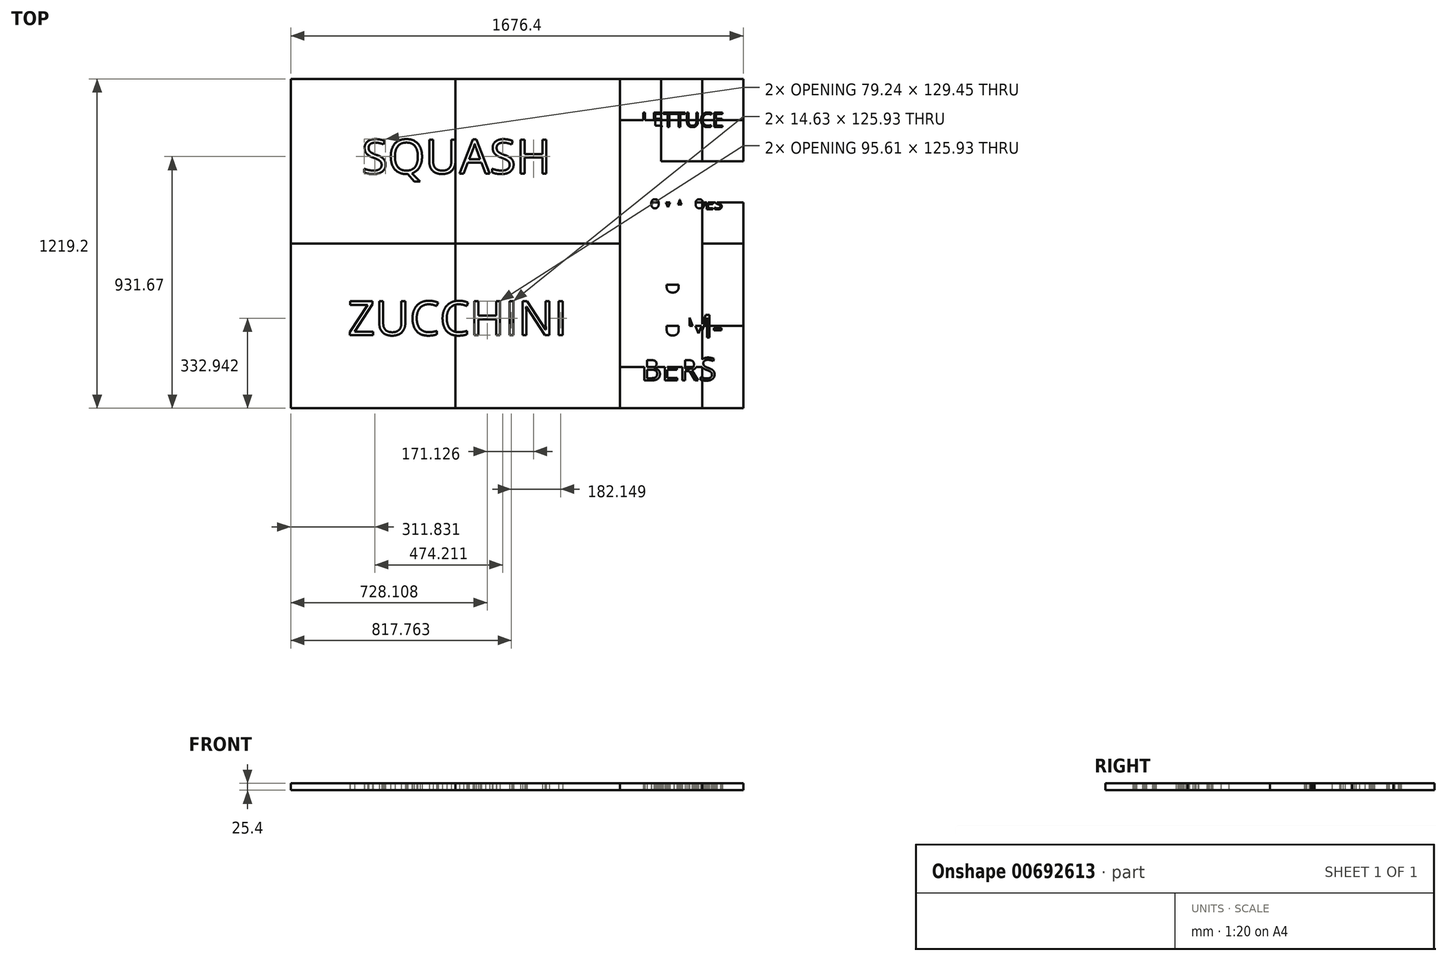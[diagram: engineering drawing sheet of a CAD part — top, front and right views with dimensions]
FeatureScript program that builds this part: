
annotation { "Feature Type Name" : "Feature", "Feature Type Description" : "" }
export const myFeature = defineFeature(function(context is Context, id is Id, definition is map)
    precondition{}
    {
        {
            var Q0;
            Q0=qCreatedBy(makeId("Top.planeOp"),FACE);
            var sketch = newSketch(context, id + "F0", { "sketchPlane" : qUnion([Q0])});
            skLineSegment(sketch, "E0.bottom", {"start": v(-653.67, 324.32) * mm, "end": v(-44.07, 324.32) * mm});
            skLineSegment(sketch, "E0.top", {"start": v(-653.67, -285.28) * mm, "end": v(-44.07, -285.28) * mm});
            skLineSegment(sketch, "E0.left", {"start": v(-653.67, 324.32) * mm, "end": v(-653.67, -285.28) * mm});
            skLineSegment(sketch, "E0.right", {"start": v(-44.07, 324.32) * mm, "end": v(-44.07, -285.28) * mm});
            skLineSegment(sketch, "E1.bottom", {"start": v(-44.07, 324.32) * mm, "end": v(565.53, 324.32) * mm});
            skLineSegment(sketch, "E1.top", {"start": v(-44.07, -285.28) * mm, "end": v(565.53, -285.28) * mm});
            skLineSegment(sketch, "E1.right", {"start": v(565.53, 324.32) * mm, "end": v(565.53, -285.28) * mm});
            skText(sketch, "E2", { "text": "SQUASH", "fontName": "OpenSans-Regular.ttf"});
            skLineSegment(sketch, "E3.0.1.0", {"start": v(565.53, -285.28) * mm, "end": v(565.53, -894.88) * mm});
            skLineSegment(sketch, "E3.0.1.1", {"start": v(-44.07, -285.28) * mm, "end": v(-44.07, -894.88) * mm});
            skLineSegment(sketch, "E3.0.1.2", {"start": v(-44.07, -894.88) * mm, "end": v(565.53, -894.88) * mm});
            skLineSegment(sketch, "E3.0.1.4", {"start": v(-653.67, -285.28) * mm, "end": v(-653.67, -894.88) * mm});
            skLineSegment(sketch, "E3.0.1.5", {"start": v(-653.67, -894.88) * mm, "end": v(-44.07, -894.88) * mm});
            skLineSegment(sketch, "E3.0.1.7", {"start": v(-44.07, -285.28) * mm, "end": v(-44.07, -894.88) * mm});
            skLineSegment(sketch, "E3.direction1", {"start": v(-653.67, -285.28) * mm, "end": v(-636.4, -285.28) * mm, "construction": true});
            skLineSegment(sketch, "E3.direction2", {"start": v(-653.67, -285.28) * mm, "end": v(-653.67, -894.88) * mm, "construction": true});
            skText(sketch, "E4", { "text": "ZUCCHINI", "fontName": "OpenSans-Regular.ttf"});
            skLineSegment(sketch, "E5.bottom", {"start": v(565.53, 324.32) * mm, "end": v(717.93, 324.32) * mm});
            skLineSegment(sketch, "E5.top", {"start": v(565.53, 171.92) * mm, "end": v(717.93, 171.92) * mm});
            skLineSegment(sketch, "E5.left", {"start": v(565.53, 324.32) * mm, "end": v(565.53, 171.92) * mm});
            skLineSegment(sketch, "E5.right", {"start": v(717.93, 324.32) * mm, "end": v(717.93, 171.92) * mm});
            skLineSegment(sketch, "E6.top", {"start": v(565.53, 19.52) * mm, "end": v(717.93, 19.52) * mm});
            skLineSegment(sketch, "E6.left", {"start": v(565.53, 171.92) * mm, "end": v(565.53, 19.52) * mm});
            skLineSegment(sketch, "E6.right", {"start": v(717.93, 171.92) * mm, "end": v(717.93, 19.52) * mm});
            skLineSegment(sketch, "E7.bottom", {"start": v(870.33, 324.32) * mm, "end": v(1022.73, 324.32) * mm});
            skLineSegment(sketch, "E7.top", {"start": v(870.33, 171.92) * mm, "end": v(1022.73, 171.92) * mm});
            skLineSegment(sketch, "E7.left", {"start": v(870.33, 324.32) * mm, "end": v(870.33, 171.92) * mm});
            skLineSegment(sketch, "E7.right", {"start": v(1022.73, 324.32) * mm, "end": v(1022.73, 171.92) * mm});
            skLineSegment(sketch, "E8.bottom", {"start": v(717.93, 324.32) * mm, "end": v(870.33, 324.32) * mm});
            skLineSegment(sketch, "E8.top", {"start": v(717.93, 171.92) * mm, "end": v(870.33, 171.92) * mm});
            skLineSegment(sketch, "E9.top", {"start": v(717.93, 19.52) * mm, "end": v(870.33, 19.52) * mm});
            skLineSegment(sketch, "E9.right", {"start": v(870.33, 171.92) * mm, "end": v(870.33, 19.52) * mm});
            skLineSegment(sketch, "E10.top", {"start": v(870.33, 19.52) * mm, "end": v(1022.73, 19.52) * mm});
            skLineSegment(sketch, "E10.right", {"start": v(1022.73, 171.92) * mm, "end": v(1022.73, 19.52) * mm});
            skText(sketch, "E11", { "text": "LETTUCE", "fontName": "OpenSans-Regular.ttf"});
            skPoint(sketch, "E11.secondSnap0", {"position": v(870.79, 146.52) * mm});
            skLineSegment(sketch, "E12.0.1.0", {"start": v(870.33, -132.88) * mm, "end": v(1022.73, -132.88) * mm});
            skLineSegment(sketch, "E12.0.1.1", {"start": v(870.33, 19.52) * mm, "end": v(870.33, -132.88) * mm});
            skLineSegment(sketch, "E12.0.1.3", {"start": v(1022.73, -132.88) * mm, "end": v(1022.73, -285.28) * mm});
            skLineSegment(sketch, "E12.0.1.4", {"start": v(717.93, -132.88) * mm, "end": v(717.93, -285.28) * mm});
            skLineSegment(sketch, "E12.0.1.5", {"start": v(717.93, 19.52) * mm, "end": v(717.93, -132.88) * mm});
            skLineSegment(sketch, "E12.0.1.6", {"start": v(870.33, -132.88) * mm, "end": v(870.33, -285.28) * mm});
            skLineSegment(sketch, "E12.0.1.7", {"start": v(870.33, -285.28) * mm, "end": v(1022.73, -285.28) * mm});
            skPoint(sketch, "E12.0.1.8", {"position": v(870.79, -158.28) * mm});
            skLineSegment(sketch, "E12.0.1.9", {"start": v(717.93, -285.28) * mm, "end": v(870.33, -285.28) * mm});
            skLineSegment(sketch, "E12.0.1.10", {"start": v(717.93, -132.88) * mm, "end": v(870.33, -132.88) * mm});
            skLineSegment(sketch, "E12.0.1.12", {"start": v(1022.73, 19.52) * mm, "end": v(1022.73, -132.88) * mm});
            skLineSegment(sketch, "E12.0.1.13", {"start": v(870.33, -132.88) * mm, "end": v(870.33, -285.28) * mm});
            skLineSegment(sketch, "E12.0.1.14", {"start": v(870.33, -132.88) * mm, "end": v(1022.73, -132.88) * mm});
            skLineSegment(sketch, "E12.0.1.15", {"start": v(717.93, -132.88) * mm, "end": v(717.93, -285.28) * mm});
            skLineSegment(sketch, "E12.0.1.16", {"start": v(870.33, 19.52) * mm, "end": v(870.33, -132.88) * mm});
            skLineSegment(sketch, "E12.0.1.17", {"start": v(717.93, 19.52) * mm, "end": v(717.93, -132.88) * mm});
            skLineSegment(sketch, "E12.0.1.18", {"start": v(717.93, -132.88) * mm, "end": v(870.33, -132.88) * mm});
            skLineSegment(sketch, "E12.0.1.20", {"start": v(565.53, -132.88) * mm, "end": v(717.93, -132.88) * mm});
            skLineSegment(sketch, "E12.0.1.21", {"start": v(565.53, -132.88) * mm, "end": v(565.53, -285.28) * mm});
            skLineSegment(sketch, "E12.0.1.22", {"start": v(565.53, -285.28) * mm, "end": v(717.93, -285.28) * mm});
            skLineSegment(sketch, "E12.0.1.23", {"start": v(565.53, 19.52) * mm, "end": v(565.53, -132.88) * mm});
            skLineSegment(sketch, "E12.0.1.24", {"start": v(565.53, -132.88) * mm, "end": v(717.93, -132.88) * mm});
            skLineSegment(sketch, "E12.direction1", {"start": v(565.53, 19.52) * mm, "end": v(591.39, 19.52) * mm, "construction": true});
            skLineSegment(sketch, "E12.direction2", {"start": v(565.53, 19.52) * mm, "end": v(565.53, -285.28) * mm, "construction": true});
            skText(sketch, "E13", { "text": "TOMATOES", "fontName": "OpenSans-Regular.ttf"});
            skPoint(sketch, "E14", {"position": v(794.13, -132.88) * mm});
            skLineSegment(sketch, "E15.bottom", {"start": v(565.53, -285.28) * mm, "end": v(870.33, -285.28) * mm});
            skLineSegment(sketch, "E15.top", {"start": v(565.53, -437.68) * mm, "end": v(870.33, -437.68) * mm});
            skLineSegment(sketch, "E15.left", {"start": v(565.53, -285.28) * mm, "end": v(565.53, -437.68) * mm});
            skLineSegment(sketch, "E15.right", {"start": v(870.33, -285.28) * mm, "end": v(870.33, -437.68) * mm});
            skLineSegment(sketch, "E16.top", {"start": v(565.53, -590.08) * mm, "end": v(870.33, -590.08) * mm});
            skLineSegment(sketch, "E16.left", {"start": v(565.53, -437.68) * mm, "end": v(565.53, -590.08) * mm});
            skLineSegment(sketch, "E16.right", {"start": v(870.33, -437.68) * mm, "end": v(870.33, -590.08) * mm});
            skLineSegment(sketch, "E17.top", {"start": v(565.53, -742.48) * mm, "end": v(870.33, -742.48) * mm});
            skLineSegment(sketch, "E17.left", {"start": v(565.53, -590.08) * mm, "end": v(565.53, -742.48) * mm});
            skLineSegment(sketch, "E17.right", {"start": v(870.33, -590.08) * mm, "end": v(870.33, -742.48) * mm});
            skLineSegment(sketch, "E18.top", {"start": v(565.53, -894.88) * mm, "end": v(870.33, -894.88) * mm});
            skLineSegment(sketch, "E18.left", {"start": v(565.53, -742.48) * mm, "end": v(565.53, -894.88) * mm});
            skLineSegment(sketch, "E18.right", {"start": v(870.33, -742.48) * mm, "end": v(870.33, -894.88) * mm});
            skLineSegment(sketch, "E19.top", {"start": v(870.33, -590.08) * mm, "end": v(1022.73, -590.08) * mm});
            skLineSegment(sketch, "E19.left", {"start": v(870.33, -285.28) * mm, "end": v(870.33, -590.08) * mm});
            skLineSegment(sketch, "E19.right", {"start": v(1022.73, -285.28) * mm, "end": v(1022.73, -590.08) * mm});
            skLineSegment(sketch, "E20.top", {"start": v(870.33, -894.88) * mm, "end": v(1022.73, -894.88) * mm});
            skLineSegment(sketch, "E20.left", {"start": v(870.33, -590.08) * mm, "end": v(870.33, -894.88) * mm});
            skLineSegment(sketch, "E20.right", {"start": v(1022.73, -590.08) * mm, "end": v(1022.73, -894.88) * mm});
            skText(sketch, "E21", { "text": "CU-\nCUM-\nBERS", "fontName": "OpenSans-Regular.ttf"});
            const initialGuessF0  = {"E2": [-0.39058, -0.0262, 1, 0, 0.127], "E4": [-0.44234, -0.6249, 1, 0, 0.127], "E11": [0.64538, 0.14652, 1, 0, 0.0535], "E13": [0.64173, -0.15828, 1, 0, 0.04124], "E21": [0.645, -0.47423, 1, 0, 0.08417]};
            skSetInitialGuess(sketch, initialGuessF0);
            skSolve(sketch);
        }
        {
            var Q0;
            {var subQ5=sQuery(id+"F0.wireOp",EDGE,"E0.bottom");Q0=makeQuery(id+"F0.imprint","IMPRINT",FACE,{"disambiguationData":[TD([[makeQuery(id+"F0.imprint","IMPRINT",EDGE,{"derivedFrom":subQ5}),-1.0]])]});}
            var Q1;
            Q1=makeQuery(id+"F0.imprint","IMPRINT",FACE,{"disambiguationData":[TD([[makeQuery(id+"F0.imprint","IMPRINT",EDGE,{"derivedFrom":sQuery(id+"F0.wireOp",EDGE,"E2.sketch_text.stroke-37")}),1.0]])]});
            extrude(context, id + "F1", {"entities" : qUnion([Q0, Q1]), "depth" : 25.4 * mm, "offsetDistance" : 25.4 * mm});
        }
        {
            var Q0;
            Q0=makeQuery(id+"F0.imprint","IMPRINT",FACE,{"disambiguationData":[TD([[makeQuery(id+"F0.imprint","IMPRINT",EDGE,{"derivedFrom":sQuery(id+"F0.wireOp",EDGE,"E2.sketch_text.stroke-67")}),1.0]])]});
            var Q1;
            {var subQ4=sQuery(id+"F0.wireOp",EDGE,"E1.bottom");Q1=makeQuery(id+"F0.imprint","IMPRINT",FACE,{"disambiguationData":[TD([[makeQuery(id+"F0.imprint","IMPRINT",EDGE,{"derivedFrom":subQ4}),-1.0]])]});}
            extrude(context, id + "F2", {"entities" : qUnion([Q0, Q1]), "depth" : 25.4 * mm, "offsetDistance" : 25.4 * mm});
        }
        {
            var Q0;
            {var subQ0=sQuery(id+"F0.wireOp",EDGE,"E4.sketch_text.stroke-40");Q0=makeQuery(id+"F0.imprint","IMPRINT",FACE,{"disambiguationData":[TD([[makeQuery(id+"F0.imprint","IMPRINT",EDGE,{"derivedFrom":subQ0}),1.0]])]});}
            var Q1;
            Q1=makeQuery(id+"F0.imprint","IMPRINT",FACE,{"disambiguationData":[TD([[makeQuery(id+"F0.imprint","IMPRINT",EDGE,{"derivedFrom":sQuery(id+"F0.wireOp",EDGE,"E3.0.1.4")}),1.0]])]});
            extrude(context, id + "F3", {"entities" : qUnion([Q0, Q1]), "depth" : 25.4 * mm, "offsetDistance" : 25.4 * mm});
        }
        {
            var Q0;
            {var subQ1=sQuery(id+"F0.wireOp",EDGE,"E3.0.1.2");Q0=makeQuery(id+"F0.imprint","IMPRINT",FACE,{"disambiguationData":[TD([[makeQuery(id+"F0.imprint","IMPRINT",EDGE,{"derivedFrom":subQ1}),1.0]])]});}
            extrude(context, id + "F4", {"entities" : qUnion([Q0]), "depth" : 25.4 * mm, "offsetDistance" : 25.4 * mm});
        }
        {
            var Q0;
            {var subQ5=sQuery(id+"F0.wireOp",EDGE,"E11.sketch_text.stroke-11");Q0=makeQuery(id+"F0.imprint","IMPRINT",FACE,{"disambiguationData":[TD([[makeQuery(id+"F0.imprint","IMPRINT",EDGE,{"derivedFrom":subQ5}),1.0]])]});}
            var Q1;
            {var subQ8=sQuery(id+"F0.wireOp",EDGE,"E5.bottom");Q1=makeQuery(id+"F0.imprint","IMPRINT",FACE,{"disambiguationData":[TD([[makeQuery(id+"F0.imprint","IMPRINT",EDGE,{"derivedFrom":subQ8}),-1.0]])]});}
            extrude(context, id + "F5", {"entities" : qUnion([Q0, Q1]), "depth" : 25.4 * mm, "offsetDistance" : 25.4 * mm});
        }
        {
            var Q0;
            {var subQ26=sQuery(id+"F0.wireOp",EDGE,"E8.bottom");Q0=makeQuery(id+"F0.imprint","IMPRINT",FACE,{"disambiguationData":[TD([[makeQuery(id+"F0.imprint","IMPRINT",EDGE,{"derivedFrom":subQ26}),-1.0]])]});}
            extrude(context, id + "F6", {"entities" : qUnion([Q0]), "depth" : 25.4 * mm, "offsetDistance" : 25.4 * mm});
        }
        {
            var Q0;
            {var subQ10=sQuery(id+"F0.wireOp",EDGE,"E7.bottom");Q0=makeQuery(id+"F0.imprint","IMPRINT",FACE,{"disambiguationData":[TD([[makeQuery(id+"F0.imprint","IMPRINT",EDGE,{"derivedFrom":subQ10}),-1.0]])]});}
            extrude(context, id + "F7", {"entities" : qUnion([Q0]), "depth" : 25.4 * mm, "offsetDistance" : 25.4 * mm});
        }
        {
            var Q0;
            {var subQ5=sQuery(id+"F0.wireOp",EDGE,"E11.sketch_text.stroke-15");Q0=makeQuery(id+"F0.imprint","IMPRINT",FACE,{"disambiguationData":[TD([[makeQuery(id+"F0.imprint","IMPRINT",EDGE,{"derivedFrom":subQ5}),1.0]])]});}
            var Q1;
            {var subQ12=sQuery(id+"F0.wireOp",EDGE,"E6.left");Q1=makeQuery(id+"F0.imprint","IMPRINT",FACE,{"disambiguationData":[TD([[makeQuery(id+"F0.imprint","IMPRINT",EDGE,{"derivedFrom":subQ12}),1.0]])]});}
            extrude(context, id + "F8", {"entities" : qUnion([Q0, Q1]), "depth" : 25.4 * mm, "offsetDistance" : 25.4 * mm});
        }
        {
            var Q0;
            {var subQ0=sQuery(id+"F0.wireOp",EDGE,"E11.sketch_text.stroke-42");Q0=makeQuery(id+"F0.imprint","IMPRINT",FACE,{"disambiguationData":[TD([[makeQuery(id+"F0.imprint","IMPRINT",EDGE,{"derivedFrom":subQ0}),1.0]])]});}
            var Q1;
            {var subQ20=sQuery(id+"F0.wireOp",EDGE,"E11.sketch_text.stroke-17");Q1=makeQuery(id+"F0.imprint","IMPRINT",FACE,{"disambiguationData":[TD([[makeQuery(id+"F0.imprint","IMPRINT",EDGE,{"derivedFrom":subQ20}),1.0]])]});}
            extrude(context, id + "F9", {"entities" : qUnion([Q0, Q1]), "depth" : 25.4 * mm, "offsetDistance" : 25.4 * mm});
        }
        {
            var Q0;
            {var subQ11=sQuery(id+"F0.wireOp",EDGE,"E10.right");Q0=makeQuery(id+"F0.imprint","IMPRINT",FACE,{"disambiguationData":[TD([[makeQuery(id+"F0.imprint","IMPRINT",EDGE,{"derivedFrom":subQ11}),-1.0]])]});}
            extrude(context, id + "F10", {"entities" : qUnion([Q0]), "depth" : 25.4 * mm, "offsetDistance" : 25.4 * mm});
        }
        {
            var Q0;
            {var subQ0=sQuery(id+"F0.wireOp",EDGE,"E13.sketch_text.stroke-21");Q0=makeQuery(id+"F0.imprint","IMPRINT",FACE,{"disambiguationData":[TD([[makeQuery(id+"F0.imprint","IMPRINT",EDGE,{"derivedFrom":subQ0}),1.0]])]});}
            var Q1;
            {var subQ4=sQuery(id+"F0.wireOp",EDGE,"E12.0.1.17");Q1=makeQuery(id+"F0.imprint","IMPRINT",FACE,{"disambiguationData":[TD([[makeQuery(id+"F0.imprint","IMPRINT",EDGE,{"derivedFrom":subQ4}),-1.0]])]});}
            extrude(context, id + "F11", {"entities" : qUnion([Q0, Q1]), "depth" : 25.4 * mm, "offsetDistance" : 25.4 * mm});
        }
        {
            var Q0;
            {var subQ1=sQuery(id+"F0.wireOp",EDGE,"E13.sketch_text.stroke-51");Q0=makeQuery(id+"F0.imprint","IMPRINT",FACE,{"disambiguationData":[TD([[makeQuery(id+"F0.imprint","IMPRINT",EDGE,{"derivedFrom":subQ1}),1.0]])]});}
            var Q1;
            {var subQ18=sQuery(id+"F0.wireOp",EDGE,"E9.top");Q1=makeQuery(id+"F0.imprint","IMPRINT",FACE,{"disambiguationData":[TD([[makeQuery(id+"F0.imprint","IMPRINT",EDGE,{"derivedFrom":subQ18}),-1.0]])]});}
            var Q2;
            {var subQ0=sQuery(id+"F0.wireOp",EDGE,"E13.sketch_text.stroke-76");Q2=makeQuery(id+"F0.imprint","IMPRINT",FACE,{"disambiguationData":[TD([[makeQuery(id+"F0.imprint","IMPRINT",EDGE,{"derivedFrom":subQ0}),1.0]])]});}
            extrude(context, id + "F12", {"entities" : qUnion([Q0, Q1, Q2]), "depth" : 25.4 * mm, "offsetDistance" : 25.4 * mm});
        }
        {
            var Q0;
            {var subQ1=sQuery(id+"F0.wireOp",EDGE,"E12.0.1.14");var subQ3=sQuery(id+"F0.wireOp",EDGE,"E13.sketch_text.stroke-75");var subQ4=makeQuery(id+"F0.imprint","INTERSECT",VERTEX,{"derivedFrom":[subQ1,subQ3]});Q0=makeQuery(id+"F0.imprint","IMPRINT",FACE,{"disambiguationData":[TD([[makeQuery(id+"F0.imprint","IMPRINT",EDGE,{"disambiguationData":[TD([[subQ4,-1.0]])],"derivedFrom":subQ3}),1.0]])]});}
            var Q1;
            {var subQ1=sQuery(id+"F0.wireOp",EDGE,"E10.top");Q1=makeQuery(id+"F0.imprint","IMPRINT",FACE,{"disambiguationData":[TD([[makeQuery(id+"F0.imprint","IMPRINT",EDGE,{"derivedFrom":subQ1}),-1.0]])]});}
            extrude(context, id + "F13", {"entities" : qUnion([Q0, Q1]), "depth" : 25.4 * mm, "offsetDistance" : 25.4 * mm});
        }
        {
            var Q0;
            {var subQ0=sQuery(id+"F0.wireOp",EDGE,"E13.sketch_text.stroke-16");Q0=makeQuery(id+"F0.imprint","IMPRINT",FACE,{"disambiguationData":[TD([[makeQuery(id+"F0.imprint","IMPRINT",EDGE,{"derivedFrom":subQ0}),1.0]])]});}
            var Q1;
            {var subQ7=sQuery(id+"F0.wireOp",EDGE,"E12.0.1.15");Q1=makeQuery(id+"F0.imprint","IMPRINT",FACE,{"disambiguationData":[TD([[makeQuery(id+"F0.imprint","IMPRINT",EDGE,{"derivedFrom":subQ7}),-1.0]])]});}
            var Q2;
            {var subQ3=sQuery(id+"F0.wireOp",EDGE,"E13.sketch_text.stroke-74");var subQ5=sQuery(id+"F0.wireOp",EDGE,"E13.sketch_text.stroke-75");var subQ7=makeQuery(id+"F0.imprint","INTERSECT",VERTEX,{"derivedFrom":[subQ3,subQ5]});Q2=makeQuery(id+"F0.imprint","IMPRINT",FACE,{"disambiguationData":[TD([[makeQuery(id+"F0.imprint","IMPRINT",EDGE,{"disambiguationData":[TD([[subQ7,1.0]])],"derivedFrom":subQ3}),1.0]])]});}
            var Q3;
            {var subQ11=sQuery(id+"F0.wireOp",EDGE,"E12.0.1.3");Q3=makeQuery(id+"F0.imprint","IMPRINT",FACE,{"disambiguationData":[TD([[makeQuery(id+"F0.imprint","IMPRINT",EDGE,{"derivedFrom":subQ11}),-1.0]])]});}
            var Q4;
            {var subQ0=sQuery(id+"F0.wireOp",EDGE,"E21.sketch_text.stroke-23");Q4=makeQuery(id+"F0.imprint","IMPRINT",FACE,{"disambiguationData":[TD([[makeQuery(id+"F0.imprint","IMPRINT",EDGE,{"derivedFrom":subQ0}),1.0]])]});}
            var Q5;
            {var subQ26=sQuery(id+"F0.wireOp",EDGE,"E16.left");Q5=makeQuery(id+"F0.imprint","IMPRINT",FACE,{"disambiguationData":[TD([[makeQuery(id+"F0.imprint","IMPRINT",EDGE,{"derivedFrom":subQ26}),1.0]])]});}
            var Q6;
            Q6=makeQuery(id+"F0.imprint","IMPRINT",FACE,{"disambiguationData":[TD([[makeQuery(id+"F0.imprint","IMPRINT",EDGE,{"derivedFrom":sQuery(id+"F0.wireOp",EDGE,"E21.sketch_text.stroke-102")}),1.0]])]});
            var Q7;
            {var subQ6=sQuery(id+"F0.wireOp",EDGE,"E21.sketch_text.stroke-132");Q7=makeQuery(id+"F0.imprint","IMPRINT",FACE,{"disambiguationData":[TD([[makeQuery(id+"F0.imprint","IMPRINT",EDGE,{"derivedFrom":subQ6}),1.0]])]});}
            var Q8;
            {var subQ25=sQuery(id+"F0.wireOp",EDGE,"E18.top");Q8=makeQuery(id+"F0.imprint","IMPRINT",FACE,{"disambiguationData":[TD([[makeQuery(id+"F0.imprint","IMPRINT",EDGE,{"derivedFrom":subQ25}),1.0]])]});}
            extrude(context, id + "F14", {"entities" : qUnion([Q0, Q1, Q2, Q3, Q4, Q5, Q6, Q7, Q8]), "depth" : 25.4 * mm, "offsetDistance" : 25.4 * mm});
        }
        {
            var Q0;
            {var subQ5=sQuery(id+"F0.wireOp",EDGE,"E13.sketch_text.stroke-54");Q0=makeQuery(id+"F0.imprint","IMPRINT",FACE,{"disambiguationData":[TD([[makeQuery(id+"F0.imprint","IMPRINT",EDGE,{"derivedFrom":subQ5}),1.0]])]});}
            var Q1;
            {var subQ0=sQuery(id+"F0.wireOp",EDGE,"E13.sketch_text.stroke-71");Q1=makeQuery(id+"F0.imprint","IMPRINT",FACE,{"disambiguationData":[TD([[makeQuery(id+"F0.imprint","IMPRINT",EDGE,{"derivedFrom":subQ0}),1.0]])]});}
            var Q2;
            {var subQ4=sQuery(id+"F0.wireOp",EDGE,"E12.0.1.15");Q2=makeQuery(id+"F0.imprint","IMPRINT",FACE,{"disambiguationData":[TD([[makeQuery(id+"F0.imprint","IMPRINT",EDGE,{"derivedFrom":subQ4}),1.0]])]});}
            var Q3;
            {var subQ1=sQuery(id+"F0.wireOp",EDGE,"E21.sketch_text.stroke-76");Q3=makeQuery(id+"F0.imprint","IMPRINT",FACE,{"disambiguationData":[TD([[makeQuery(id+"F0.imprint","IMPRINT",EDGE,{"derivedFrom":subQ1}),1.0]])]});}
            var Q4;
            {var subQ5=sQuery(id+"F0.wireOp",EDGE,"E12.0.1.7");Q4=makeQuery(id+"F0.imprint","IMPRINT",FACE,{"disambiguationData":[TD([[makeQuery(id+"F0.imprint","IMPRINT",EDGE,{"derivedFrom":subQ5}),-1.0]])]});}
            var Q5;
            {var subQ0=sQuery(id+"F0.wireOp",EDGE,"E21.sketch_text.stroke-97");Q5=makeQuery(id+"F0.imprint","IMPRINT",FACE,{"disambiguationData":[TD([[makeQuery(id+"F0.imprint","IMPRINT",EDGE,{"derivedFrom":subQ0}),1.0]])]});}
            var Q6;
            {var subQ0=sQuery(id+"F0.wireOp",EDGE,"E21.sketch_text.stroke-135");Q6=makeQuery(id+"F0.imprint","IMPRINT",FACE,{"disambiguationData":[TD([[makeQuery(id+"F0.imprint","IMPRINT",EDGE,{"derivedFrom":subQ0}),1.0]])]});}
            var Q7;
            {var subQ0=sQuery(id+"F0.wireOp",EDGE,"E21.sketch_text.stroke-56");Q7=makeQuery(id+"F0.imprint","IMPRINT",FACE,{"disambiguationData":[TD([[makeQuery(id+"F0.imprint","IMPRINT",EDGE,{"derivedFrom":subQ0}),1.0]])]});}
            var Q8;
            {var subQ34=sQuery(id+"F0.wireOp",EDGE,"E17.left");Q8=makeQuery(id+"F0.imprint","IMPRINT",FACE,{"disambiguationData":[TD([[makeQuery(id+"F0.imprint","IMPRINT",EDGE,{"derivedFrom":subQ34}),1.0]])]});}
            var Q9;
            {var subQ5=sQuery(id+"F0.wireOp",EDGE,"E13.sketch_text.stroke-32");Q9=makeQuery(id+"F0.imprint","IMPRINT",FACE,{"disambiguationData":[TD([[makeQuery(id+"F0.imprint","IMPRINT",EDGE,{"derivedFrom":subQ5}),1.0]])]});}
            extrude(context, id + "F15", {"entities" : qUnion([Q0, Q1, Q2, Q3, Q4, Q5, Q6, Q7, Q8, Q9]), "depth" : 25.4 * mm, "offsetDistance" : 25.4 * mm});
        }
        {
            var Q0;
            {var subQ1=sQuery(id+"F0.wireOp",EDGE,"E21.sketch_text.stroke-63");Q0=makeQuery(id+"F0.imprint","IMPRINT",FACE,{"disambiguationData":[TD([[makeQuery(id+"F0.imprint","IMPRINT",EDGE,{"derivedFrom":subQ1}),1.0]])]});}
            var Q1;
            {var subQ5=sQuery(id+"F0.wireOp",EDGE,"E21.sketch_text.stroke-70");Q1=makeQuery(id+"F0.imprint","IMPRINT",FACE,{"disambiguationData":[TD([[makeQuery(id+"F0.imprint","IMPRINT",EDGE,{"derivedFrom":subQ5}),1.0]])]});}
            var Q2;
            {var subQ11=sQuery(id+"F0.wireOp",EDGE,"E20.top");Q2=makeQuery(id+"F0.imprint","IMPRINT",FACE,{"disambiguationData":[TD([[makeQuery(id+"F0.imprint","IMPRINT",EDGE,{"derivedFrom":subQ11}),1.0]])]});}
            var Q3;
            {var subQ0=sQuery(id+"F0.wireOp",EDGE,"E21.sketch_text.stroke-144");Q3=makeQuery(id+"F0.imprint","IMPRINT",FACE,{"disambiguationData":[TD([[makeQuery(id+"F0.imprint","IMPRINT",EDGE,{"derivedFrom":subQ0}),1.0]])]});}
            var Q4;
            {var subQ13=sQuery(id+"F0.wireOp",EDGE,"E15.left");Q4=makeQuery(id+"F0.imprint","IMPRINT",FACE,{"disambiguationData":[TD([[makeQuery(id+"F0.imprint","IMPRINT",EDGE,{"derivedFrom":subQ13}),1.0]])]});}
            extrude(context, id + "F16", {"entities" : qUnion([Q0, Q1, Q2, Q3, Q4]), "depth" : 25.4 * mm, "offsetDistance" : 25.4 * mm});
        }
    });
